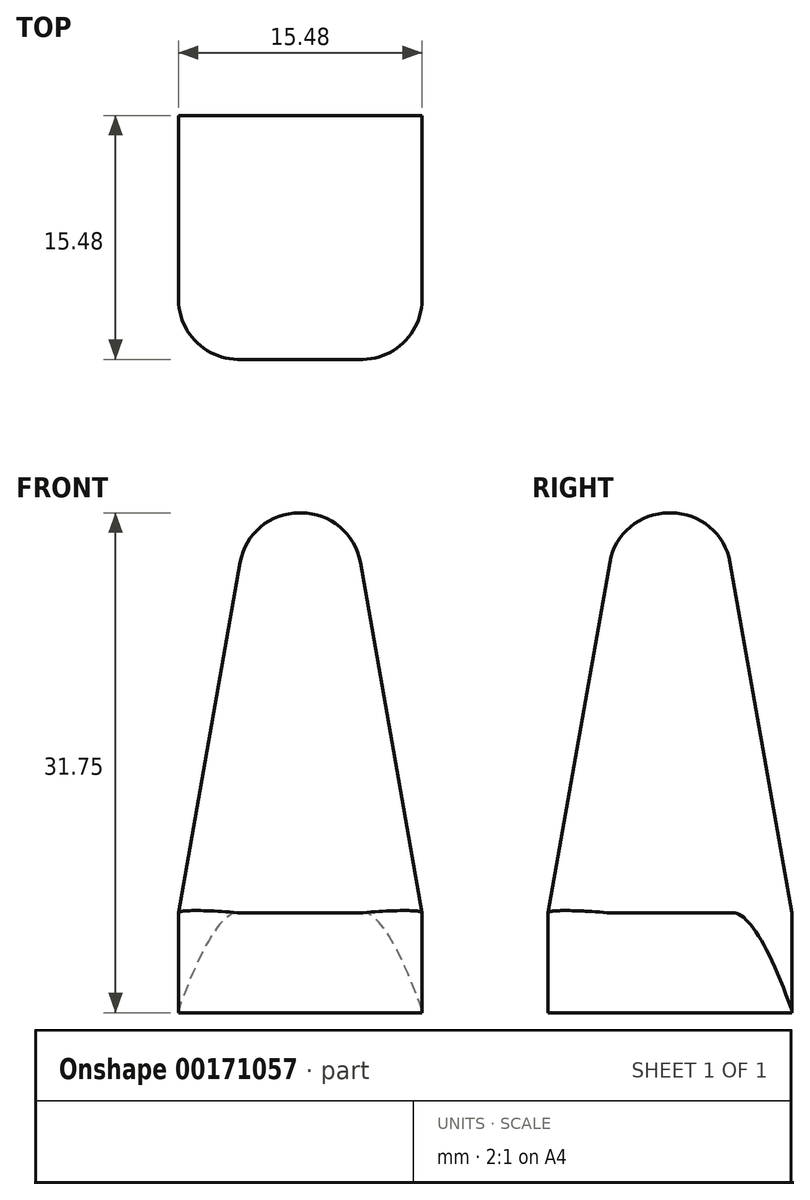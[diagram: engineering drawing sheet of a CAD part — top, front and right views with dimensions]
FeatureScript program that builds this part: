
annotation { "Feature Type Name" : "Feature", "Feature Type Description" : "" }
export const myFeature = defineFeature(function(context is Context, id is Id, definition is map)
    precondition{}
    {
        {
            var Q0;
            Q0=qCreatedBy(makeId("Top.planeOp"),FACE);
            var sketch = newSketch(context, id + "F0", { "sketchPlane" : qUnion([Q0])});
            skLineSegment(sketch, "E0.bottom", {"start": v(0, 0) * mm, "end": v(15.48, 0) * mm});
            skLineSegment(sketch, "E0.top", {"start": v(0, 15.48) * mm, "end": v(15.48, 15.48) * mm});
            skLineSegment(sketch, "E0.left", {"start": v(0, 0) * mm, "end": v(0, 15.48) * mm});
            skLineSegment(sketch, "E0.right", {"start": v(15.48, 0) * mm, "end": v(15.48, 15.48) * mm});
            skSolve(sketch);
        }
        {
            var Q0;
            Q0 = qSketchRegion(id + "F0", true);
            extrude(context, id + "F1", {"entities" : qUnion([Q0]), "oppositeDirection" : true, "depth" : 6.35 * mm});
        }
        {
            var Q0;
            Q0 = qSketchRegion(id + "F0", true);
            extrude(context, id + "F2", {"entities" : qUnion([Q0]), "operationType" : NewBodyOperationType.ADD, "depth" : 25.4 * mm, "hasDraft" : true, "draftAngle" : 10 * degree, "draftPullDirection" : true});
        }
        {
            var Q0;
            Q0=makeQuery(id+"F2.opExtrude","SWEPT_EDGE",EDGE,{"disambiguationData":[OSD([sQuery(id+"F0.wireOp",EDGE,"E0.top"),sQuery(id+"F0.wireOp",EDGE,"E0.right")])]});
            var Q1;
            Q1=makeQuery(id+"F2.opExtrude","SWEPT_EDGE",EDGE,{"disambiguationData":[OSD([sQuery(id+"F0.wireOp",EDGE,"E0.top"),sQuery(id+"F0.wireOp",EDGE,"E0.left")])]});
            var Q2;
            Q2=makeQuery(id+"F2.opExtrude","SWEPT_EDGE",EDGE,{"disambiguationData":[OSD([sQuery(id+"F0.wireOp",EDGE,"E0.bottom"),sQuery(id+"F0.wireOp",EDGE,"E0.right")])]});
            var Q3;
            Q3=makeQuery(id+"F2.opExtrude","SWEPT_EDGE",EDGE,{"disambiguationData":[OSD([sQuery(id+"F0.wireOp",EDGE,"E0.bottom"),sQuery(id+"F0.wireOp",EDGE,"E0.left")])]});
            var Q4;
            Q4=makeQuery(id+"F1.opExtrude","SWEPT_EDGE",EDGE,{"disambiguationData":[OSD([sQuery(id+"F0.wireOp",EDGE,"E0.bottom"),sQuery(id+"F0.wireOp",EDGE,"E0.left")])]});
            var Q5;
            Q5=makeQuery(id+"F1.opExtrude","SWEPT_EDGE",EDGE,{"disambiguationData":[OSD([sQuery(id+"F0.wireOp",EDGE,"E0.bottom"),sQuery(id+"F0.wireOp",EDGE,"E0.right")])]});
            var Q6;
            Q6=makeQuery(id+"F2.opExtrude","CAP_EDGE",EDGE,{"disambiguationData":[OSD([sQuery(id+"F0.wireOp",EDGE,"E0.right")])],"isStart":false});
            var Q7;
            Q7=makeQuery(id+"F2.opExtrude","CAP_EDGE",EDGE,{"disambiguationData":[OSD([sQuery(id+"F0.wireOp",EDGE,"E0.bottom")])],"isStart":false});
            var Q8;
            Q8=makeQuery(id+"F2.opExtrude","CAP_EDGE",EDGE,{"disambiguationData":[OSD([sQuery(id+"F0.wireOp",EDGE,"E0.left")])],"isStart":false});
            var Q9;
            Q9=makeQuery(id+"F2.opExtrude","CAP_EDGE",EDGE,{"disambiguationData":[OSD([sQuery(id+"F0.wireOp",EDGE,"E0.top")])],"isStart":false});
            fillet(context, id + "F3", {"entities" : qUnion([Q0, Q1, Q2, Q3, Q4, Q5, Q6, Q7, Q8, Q9]), "radius" : 3.8 * mm, "tangentPropagation" : true, "allowEdgeOverflow" : false});
        }
    });
